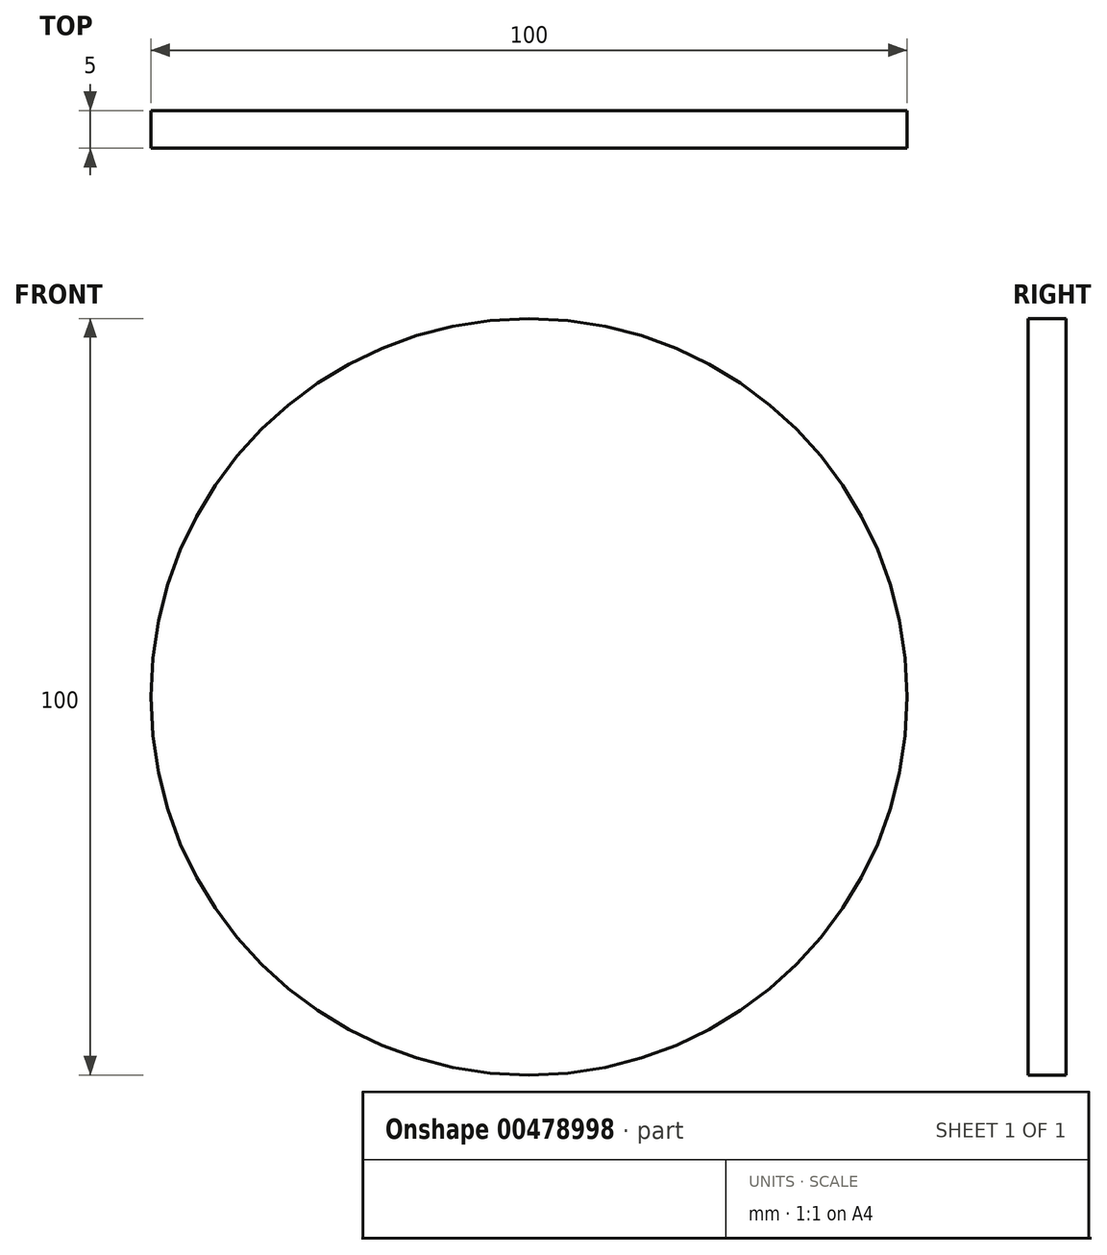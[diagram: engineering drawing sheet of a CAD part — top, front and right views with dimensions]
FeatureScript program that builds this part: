
annotation { "Feature Type Name" : "Feature", "Feature Type Description" : "" }
export const myFeature = defineFeature(function(context is Context, id is Id, definition is map)
    precondition{}
    {
        {
            var Q0;
            Q0=qCreatedBy(makeId("Front.planeOp"),FACE);
            var sketch = newSketch(context, id + "F0", { "sketchPlane" : qUnion([Q0])});
            skCircle(sketch, "E0", {"center": v(0, 0) * mm, "radius": 50 * mm});
            skSolve(sketch);
        }
        {
            var Q0;
            Q0=makeQuery(id+"F0.imprint","IMPRINT",FACE,{"disambiguationData":[TD([[makeQuery(id+"F0.imprint","IMPRINT",EDGE,{"derivedFrom":sQuery(id+"F0.wireOp",EDGE,"E0")}),1.0]])]});
            extrude(context, id + "F1", {"entities" : qUnion([Q0]), "depth" : 5 * mm});
        }
    });
